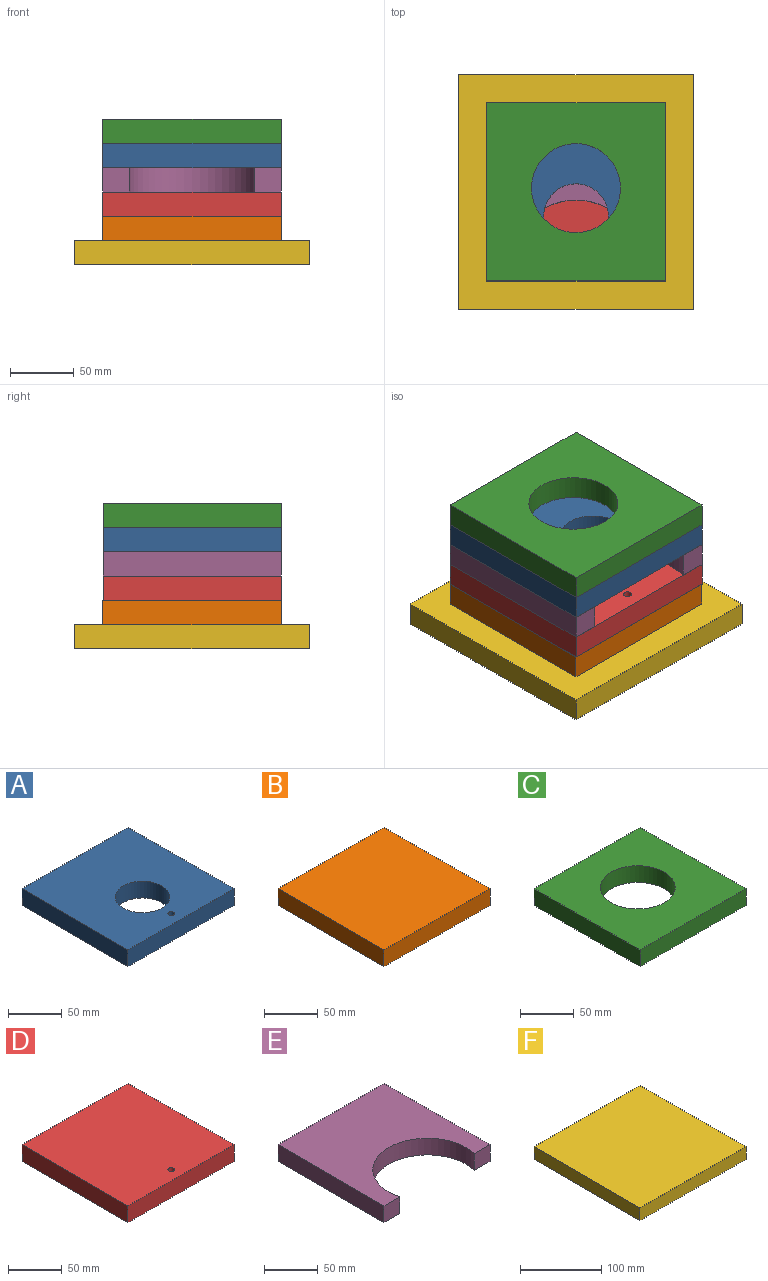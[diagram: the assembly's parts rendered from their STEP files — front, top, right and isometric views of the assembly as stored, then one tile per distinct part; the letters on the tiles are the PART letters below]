
ASSEMBLY  parts=6 mates=5
PART A: 8 faces, bbox 139.7x139.7x19.1 mm
  f0: plane 139.7x19.05mm, normal (0,-1,0), area 2661.3mm2, adj f1,f5,f6,f7
  f1: plane 139.7x19.05mm, normal (1,0,0), area 2661.3mm2, adj f0,f2,f6,f7
  f2: plane 139.7x19.05mm, normal (0,1,0), area 2661.3mm2, adj f1,f5,f6,f7
  f3: cylinder r=25.4mm len=50.8mm, axis (0,0,-1), area 3040.2mm2, adj f6,f7
  f4: cylinder r=3.17mm len=19.05mm, axis (0,0,-1), area 380mm2, adj f6,f7
  f5: plane 139.7x19.05mm, normal (-1,0,0), area 2661.3mm2, adj f0,f2,f6,f7
  f6: plane 139.7x139.7mm, normal (0,0,1), area 17457.6mm2, adj f0,f1,f2,f3,f4,f5
  f7: plane 139.7x139.7mm, normal (0,0,-1), area 17457.6mm2, adj f0,f1,f2,f3,f4,f5
PART B: 6 faces, bbox 139.7x139.7x19.1 mm
  f0: plane 139.7x19.05mm, normal (-1,0,0), area 2661.3mm2, adj f1,f3,f4,f5
  f1: plane 139.7x19.05mm, normal (0,-1,0), area 2661.3mm2, adj f0,f2,f4,f5
  f2: plane 139.7x19.05mm, normal (1,0,0), area 2661.3mm2, adj f1,f3,f4,f5
  f3: plane 139.7x19.05mm, normal (0,1,0), area 2661.3mm2, adj f0,f2,f4,f5
  f4: plane 139.7x139.7mm, normal (0,0,1), area 19516.1mm2, adj f0,f1,f2,f3
  f5: plane 139.7x139.7mm, normal (0,0,-1), area 19516.1mm2, adj f0,f1,f2,f3
PART C: 7 faces, bbox 139.7x139.7x19.1 mm
  f0: plane 139.7x19.05mm, normal (-1,0,0), area 2661.3mm2, adj f1,f4,f5,f6
  f1: plane 139.7x19.05mm, normal (0,-1,0), area 2661.3mm2, adj f0,f2,f5,f6
  f2: plane 139.7x19.05mm, normal (1,0,0), area 2661.3mm2, adj f1,f4,f5,f6
  f3: cylinder r=34.92mm len=69.85mm, axis (0,0,-1), area 4180.3mm2, adj f5,f6
  f4: plane 139.7x19.05mm, normal (0,1,0), area 2661.3mm2, adj f0,f2,f5,f6
  f5: plane 139.7x139.7mm, normal (0,0,1), area 15684.1mm2, adj f0,f1,f2,f3,f4
  f6: plane 139.7x139.7mm, normal (0,0,-1), area 15684.1mm2, adj f0,f1,f2,f3,f4
PART D: 7 faces, bbox 139.7x139.7x19.1 mm
  f0: plane 139.7x19.05mm, normal (0,-1,0), area 2661.3mm2, adj f1,f4,f5,f6
  f1: plane 139.7x19.05mm, normal (1,0,0), area 2661.3mm2, adj f0,f2,f5,f6
  f2: plane 139.7x19.05mm, normal (0,1,0), area 2661.3mm2, adj f1,f4,f5,f6
  f3: cylinder r=3.17mm len=19.05mm, axis (0,0,-1), area 380mm2, adj f5,f6
  f4: plane 139.7x19.05mm, normal (-1,0,0), area 2661.3mm2, adj f0,f2,f5,f6
  f5: plane 139.7x139.7mm, normal (0,0,1), area 19484.4mm2, adj f0,f1,f2,f3,f4
  f6: plane 139.7x139.7mm, normal (0,0,-1), area 19484.4mm2, adj f0,f1,f2,f3,f4
PART E: 8 faces, bbox 139.7x139.7x19.1 mm
  f0: cylinder r=50.8mm len=101.6mm, axis (0,0,-1), area 3529.3mm2, adj f1,f5,f6,f7
  f1: plane 20.66x19.05mm, normal (0,-1,0), area 393.6mm2, adj f0,f2,f6,f7
  f2: plane 139.7x19.05mm, normal (1,0,0), area 2661.3mm2, adj f1,f3,f6,f7
  f3: plane 139.7x19.05mm, normal (0,1,0), area 2661.3mm2, adj f2,f4,f6,f7
  f4: plane 139.7x19.05mm, normal (-1,0,0), area 2661.3mm2, adj f3,f5,f6,f7
  f5: plane 20.66x19.05mm, normal (0,-1,0), area 393.6mm2, adj f0,f4,f6,f7
  f6: plane 139.7x139.7mm, normal (0,0,1), area 14185.7mm2, adj f0,f1,f2,f3,f4,f5
  f7: plane 139.7x139.7mm, normal (0,0,-1), area 14185.7mm2, adj f0,f1,f2,f3,f4,f5
PART F: 6 faces, bbox 184.2x184.2x19.1 mm
  f0: plane 184.15x19.05mm, normal (0,-1,0), area 3508.1mm2, adj f1,f3,f4,f5
  f1: plane 184.15x19.05mm, normal (1,0,0), area 3508.1mm2, adj f0,f2,f4,f5
  f2: plane 184.15x19.05mm, normal (0,1,0), area 3508.1mm2, adj f1,f3,f4,f5
  f3: plane 184.15x19.05mm, normal (-1,0,0), area 3508.1mm2, adj f0,f2,f4,f5
  f4: plane 184.15x184.15mm, normal (0,0,1), area 33911.2mm2, adj f0,f1,f2,f3
  f5: plane 184.15x184.15mm, normal (0,0,-1), area 33911.2mm2, adj f0,f1,f2,f3
PLACE A t=(-189.59,-76.15,103.91)mm
PLACE B t=(-189.59,-76.06,46.76)mm
PLACE C t=(-189.59,-73.18,122.96)mm
PLACE D t=(-189.59,-76.15,65.81)mm
PLACE E t=(-189.59,-76.15,84.86)mm
PLACE F t=(-189.59,-76.06,27.71)mm
MATE fastened D.f5 <-> E.f7  axis (0,0,1) through (-119.74,-146,84.86)mm
MATE fastened A.f6 <-> C.f6  axis (0,0,1) through (-119.74,-146,122.96)mm
MATE fastened E.f6 <-> A.f7  axis (0,0,1) through (-119.74,-146,103.91)mm
MATE fastened B.f4 <-> D.f6  axis (0,0,1) through (-189.59,-76.06,65.81)mm
MATE fastened F.f4 <-> B.f5  axis (0,0,1) through (-189.59,-76.06,46.76)mm
